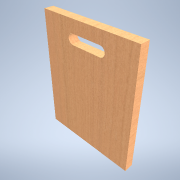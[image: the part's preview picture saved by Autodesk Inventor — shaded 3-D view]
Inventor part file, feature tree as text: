
AUTODESK INVENTOR PART (.ipt)
format: ipt  version: 2021 (Build 250183000, 183)  size: 130,560 bytes
history: native  units: mm
features: extrude x2, sketch x2
ambient origin geometry x8: Origin, YZ Plane, XZ Plane, XY Plane, X Axis, Y Axis, Z Axis, Center Point
bodies: Solid1 (feature_tree)
feature tree (4):
  extrude  "Extrusion1"  Depth=30.0mm
  extrude  "Extrusion2"  Depth=25.0mm
  sketch  "Sketch1"  dims[d3=0.0mm d4=30.0mm]
  sketch  "Sketch2"  dims[d5=20.0mm d6=25.0mm d7=19.05mm d8=0.0mm]
